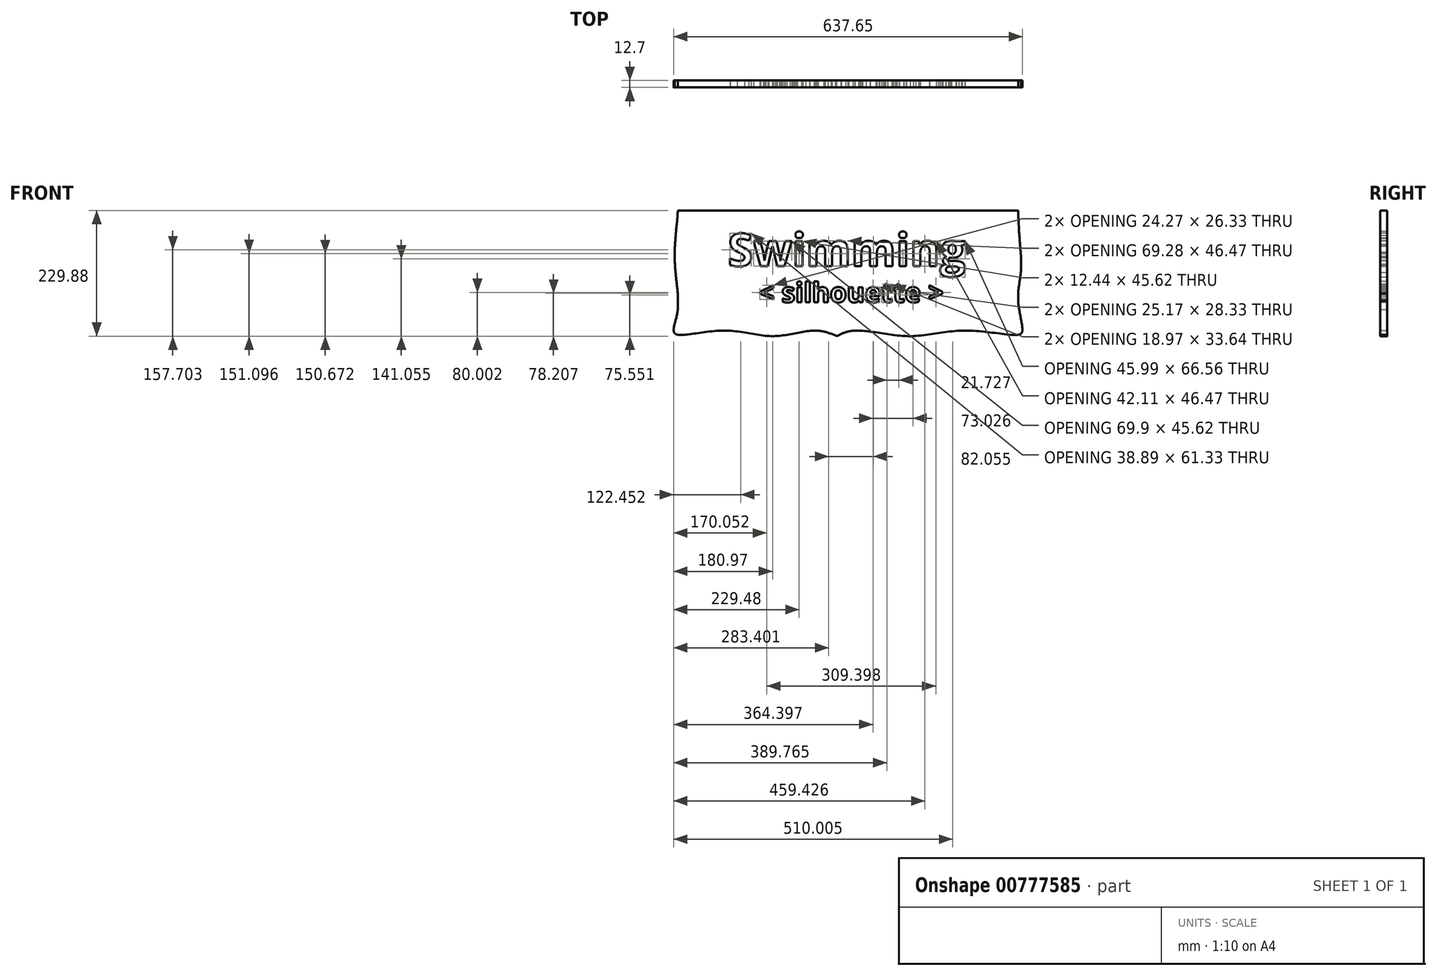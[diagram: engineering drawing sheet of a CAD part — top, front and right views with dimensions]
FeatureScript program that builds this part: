
annotation { "Feature Type Name" : "Feature", "Feature Type Description" : "" }
export const myFeature = defineFeature(function(context is Context, id is Id, definition is map)
    precondition{}
    {
        {
            var Q0;
            Q0=qCreatedBy(makeId("Front.planeOp"),FACE);
            var sketch = newSketch(context, id + "F0", { "sketchPlane" : qUnion([Q0])});
            skLineSegment(sketch, "E0.bottom", {"start": v(-290.57, 105.94) * mm, "end": v(331.73, 105.94) * mm});
            skLineSegment(sketch, "E0.top", {"start": v(-290.57, -113.77) * mm, "end": v(331.73, -113.77) * mm});
            skLineSegment(sketch, "E0.left", {"start": v(-290.57, 105.94) * mm, "end": v(-290.57, -113.77) * mm});
            skLineSegment(sketch, "E0.right", {"start": v(331.73, 105.94) * mm, "end": v(331.73, -113.77) * mm});
            skPoint(sketch, "E1", {"position": v(20.58, 105.94) * mm});
            skSolve(sketch);
        }
        {
            var Q0;
            Q0=makeQuery(id+"F0.imprint","IMPRINT",FACE,{"disambiguationData":[TD([[makeQuery(id+"F0.imprint","IMPRINT",EDGE,{"derivedFrom":sQuery(id+"F0.wireOp",EDGE,"E0.bottom")}),-1.0]])]});
            extrude(context, id + "F1", {"entities" : qUnion([Q0]), "depth" : 12.7 * mm, "offsetDistance" : 25.4 * mm});
        }
        {
            var Q0;
            Q0=makeQuery(id+"F1.opExtrude","CAP_FACE",FACE,{"disambiguationData":[OSD([sQuery(id+"F0.wireOp",EDGE,"E0.bottom"),sQuery(id+"F0.wireOp",EDGE,"E0.top"),sQuery(id+"F0.wireOp",EDGE,"E0.left"),sQuery(id+"F0.wireOp",EDGE,"E0.right")])],"isStart":false});
            var sketch = newSketch(context, id + "F2", { "sketchPlane" : qUnion([Q0])});
            skText(sketch, "E2", { "text": "Swimming", "fontName": "OpenSans-Bold.ttf"});
            const initialGuessF2  = {"E2": [-0.19905, 0.00392, 1, 0, 0.06017]};
            skSetInitialGuess(sketch, initialGuessF2);
            skSolve(sketch);
        }
        {
            var Q0;
            Q0=makeQuery(id+"F2.imprint","IMPRINT",FACE,{"disambiguationData":[TD([[makeQuery(id+"F2.imprint","IMPRINT",EDGE,{"derivedFrom":sQuery(id+"F2.wireOp",EDGE,"E2.sketch_text.stroke-0")}),1.0]])]});
            var sketch = newSketch(context, id + "F3", { "sketchPlane" : qUnion([Q0])});
            skText(sketch, "E3", { "text": " < silhouette >", "fontName": "OpenSans-Bold.ttf"});
            const initialGuessF3  = {"E3": [-0.15546, -0.06206, 1, 0, 0.03604]};
            skSetInitialGuess(sketch, initialGuessF3);
            skSolve(sketch);
        }
        {
            var Q0;
            Q0=qSketchRegion(id+"F2",true);
            var Q1;
            Q1=qSketchRegion(id+"F3",true);
            extrude(context, id + "F4", {"entities" : qUnion([Q0, Q1]), "operationType" : NewBodyOperationType.REMOVE, "oppositeDirection" : true, "depth" : 25.4 * mm, "offsetDistance" : 25.4 * mm});
        }
        {
            var Q0;
            {var subQ0=sQuery(id+"F0.wireOp",EDGE,"E0.right");var subQ1=sQuery(id+"F0.wireOp",EDGE,"E0.bottom");var subQ2=sQuery(id+"F0.wireOp",EDGE,"E0.left");var subQ3=sQuery(id+"F0.wireOp",EDGE,"E0.top");Q0=makeQuery(id+"F4.boolean.opBoolean","SPLIT",FACE,{"disambiguationData":[TD([makeQuery(id+"F1.opExtrude","SWEPT_FACE",FACE,{"disambiguationData":[OSD([subQ1])]})])],"derivedFrom":makeQuery(id+"F1.opExtrude","CAP_FACE",FACE,{"disambiguationData":[OSD([subQ1,subQ3,subQ2,subQ0])],"isStart":false})});}
            var sketch = newSketch(context, id + "F5", { "sketchPlane" : qUnion([Q0])});
            skPoint(sketch, "E4", {"position": v(-290.57, -75.67) * mm});
            skPoint(sketch, "E5", {"position": v(-290.57, 4.34) * mm});
            skPoint(sketch, "E6", {"position": v(-290.57, 74.2) * mm});
            skLineSegment(sketch, "E7", {"start": v(-290.57, 74.2) * mm, "end": v(-293.1, 74.2) * mm});
            skLineSegment(sketch, "E8", {"start": v(-290.57, 4.34) * mm, "end": v(-295.65, 4.34) * mm});
            skLineSegment(sketch, "E9", {"start": v(-290.57, -113.77) * mm, "end": v(-298.19, -113.77) * mm});
            skLineSegment(sketch, "E10", {"start": v(-290.57, -113.77) * mm, "end": v(-290.57, -121.39) * mm});
            skPoint(sketch, "E11", {"position": v(-210.29, -113.77) * mm});
            skPoint(sketch, "E12", {"position": v(0, -113.77) * mm});
            skPoint(sketch, "E13", {"position": v(-39.3, -113.77) * mm});
            skPoint(sketch, "E14", {"position": v(-115.36, -113.77) * mm});
            skPoint(sketch, "E15", {"position": v(33.42, -113.77) * mm});
            skPoint(sketch, "E16", {"position": v(131.68, -113.77) * mm});
            skPoint(sketch, "E17", {"position": v(235.49, -113.77) * mm});
            skPoint(sketch, "E18", {"position": v(331.73, -59.7) * mm});
            skPoint(sketch, "E19", {"position": v(331.73, -3.91) * mm});
            skPoint(sketch, "E20", {"position": v(331.73, 54.1) * mm});
            skLineSegment(sketch, "E21", {"start": v(331.73, 54.1) * mm, "end": v(334.27, 54.1) * mm});
            skLineSegment(sketch, "E22", {"start": v(331.73, -3.91) * mm, "end": v(336.81, -3.91) * mm});
            skLineSegment(sketch, "E23", {"start": v(331.73, -113.77) * mm, "end": v(339.35, -113.77) * mm});
            skLineSegment(sketch, "E24", {"start": v(331.73, -113.77) * mm, "end": v(331.73, -121.39) * mm});
            skLineSegment(sketch, "E25", {"start": v(-115.36, -113.77) * mm, "end": v(-115.36, -123.93) * mm});
            skLineSegment(sketch, "E26", {"start": v(0, -113.77) * mm, "end": v(0, -123.93) * mm});
            skLineSegment(sketch, "E27", {"start": v(131.68, -113.77) * mm, "end": v(131.68, -123.93) * mm});
            skFitSpline(sketch, "E28", {"points": [v(-290.57, 105.94) * mm, v(-293.1, 74.2) * mm, v(-295.65, 4.34) * mm, v(-290.57, -75.67) * mm, v(-298.19, -113.77) * mm, v(-290.57, -121.39) * mm, v(-206.79, -113.77) * mm, v(-115.36, -123.93) * mm, v(-39.3, -113.77) * mm, v(0, -123.93) * mm], "startDerivative": vector(-16.13, -484.78) * mm, "endDerivative": vector(374.15, -159.82) * mm});
            skFitSpline(sketch, "E29", {"points": [v(331.73, 105.94) * mm, v(334.27, 54.1) * mm, v(336.81, -3.91) * mm, v(331.73, -59.7) * mm, v(339.35, -113.77) * mm, v(331.73, -121.39) * mm, v(235.49, -113.77) * mm, v(131.68, -123.93) * mm, v(33.42, -113.77) * mm, v(0, -123.93) * mm], "startDerivative": vector(15.9, -475.63) * mm, "endDerivative": vector(-324.26, -164.08) * mm});
            skSolve(sketch);
        }
        {
            var Q0;
            {var subQ0=sQuery(id+"F5.wireOp",EDGE,"E26");Q0=makeQuery(id+"F5.imprint","IMPRINT",FACE,{"disambiguationData":[TD([[makeQuery(id+"F5.imprint","IMPRINT",EDGE,{"derivedFrom":subQ0}),-1.0]])]});}
            var Q1;
            {var subQ0=sQuery(id+"F5.wireOp",EDGE,"E26");Q1=makeQuery(id+"F5.imprint","IMPRINT",FACE,{"disambiguationData":[TD([[makeQuery(id+"F5.imprint","IMPRINT",EDGE,{"derivedFrom":subQ0}),1.0]])]});}
            var Q2;
            {var subQ0=sQuery(id+"F5.wireOp",EDGE,"E25");Q2=makeQuery(id+"F5.imprint","IMPRINT",FACE,{"disambiguationData":[TD([[makeQuery(id+"F5.imprint","IMPRINT",EDGE,{"derivedFrom":subQ0}),1.0]])]});}
            var Q3;
            {var subQ0=sQuery(id+"F5.wireOp",EDGE,"E25");Q3=makeQuery(id+"F5.imprint","IMPRINT",FACE,{"disambiguationData":[TD([[makeQuery(id+"F5.imprint","IMPRINT",EDGE,{"derivedFrom":subQ0}),-1.0]])]});}
            var Q4;
            {var subQ0=sQuery(id+"F5.wireOp",EDGE,"E10");Q4=makeQuery(id+"F5.imprint","IMPRINT",FACE,{"disambiguationData":[TD([[makeQuery(id+"F5.imprint","IMPRINT",EDGE,{"derivedFrom":subQ0}),1.0]])]});}
            var Q5;
            {var subQ0=sQuery(id+"F5.wireOp",EDGE,"E9");Q5=makeQuery(id+"F5.imprint","IMPRINT",FACE,{"disambiguationData":[TD([[makeQuery(id+"F5.imprint","IMPRINT",EDGE,{"derivedFrom":subQ0}),1.0]])]});}
            var Q6;
            {var subQ0=sQuery(id+"F5.wireOp",EDGE,"E9");Q6=makeQuery(id+"F5.imprint","IMPRINT",FACE,{"disambiguationData":[TD([[makeQuery(id+"F5.imprint","IMPRINT",EDGE,{"derivedFrom":subQ0}),-1.0]])]});}
            var Q7;
            {var subQ0=sQuery(id+"F5.wireOp",EDGE,"E8");Q7=makeQuery(id+"F5.imprint","IMPRINT",FACE,{"disambiguationData":[TD([[makeQuery(id+"F5.imprint","IMPRINT",EDGE,{"derivedFrom":subQ0}),1.0]])]});}
            var Q8;
            {var subQ0=sQuery(id+"F5.wireOp",EDGE,"E7");Q8=makeQuery(id+"F5.imprint","IMPRINT",FACE,{"disambiguationData":[TD([[makeQuery(id+"F5.imprint","IMPRINT",EDGE,{"derivedFrom":subQ0}),1.0]])]});}
            var Q9;
            {var subQ0=makeQuery(id+"F1.opExtrude","CAP_EDGE",EDGE,{"disambiguationData":[OSD([sQuery(id+"F0.wireOp",EDGE,"E0.bottom")])],"isStart":false});Q9=makeQuery(id+"F5.imprint","IMPRINT",FACE,{"disambiguationData":[TD([[makeQuery(id+"F5.imprint","IMPRINT",EDGE,{"derivedFrom":subQ0}),-1.0]])]});}
            var Q10;
            {var subQ0=sQuery(id+"F5.wireOp",EDGE,"E27");Q10=makeQuery(id+"F5.imprint","IMPRINT",FACE,{"disambiguationData":[TD([[makeQuery(id+"F5.imprint","IMPRINT",EDGE,{"derivedFrom":subQ0}),-1.0]])]});}
            var Q11;
            {var subQ0=sQuery(id+"F5.wireOp",EDGE,"E27");Q11=makeQuery(id+"F5.imprint","IMPRINT",FACE,{"disambiguationData":[TD([[makeQuery(id+"F5.imprint","IMPRINT",EDGE,{"derivedFrom":subQ0}),1.0]])]});}
            var Q12;
            {var subQ0=sQuery(id+"F5.wireOp",EDGE,"E24");Q12=makeQuery(id+"F5.imprint","IMPRINT",FACE,{"disambiguationData":[TD([[makeQuery(id+"F5.imprint","IMPRINT",EDGE,{"derivedFrom":subQ0}),-1.0]])]});}
            var Q13;
            {var subQ0=sQuery(id+"F5.wireOp",EDGE,"E23");Q13=makeQuery(id+"F5.imprint","IMPRINT",FACE,{"disambiguationData":[TD([[makeQuery(id+"F5.imprint","IMPRINT",EDGE,{"derivedFrom":subQ0}),-1.0]])]});}
            var Q14;
            {var subQ0=sQuery(id+"F5.wireOp",EDGE,"E23");Q14=makeQuery(id+"F5.imprint","IMPRINT",FACE,{"disambiguationData":[TD([[makeQuery(id+"F5.imprint","IMPRINT",EDGE,{"derivedFrom":subQ0}),1.0]])]});}
            var Q15;
            {var subQ0=sQuery(id+"F5.wireOp",EDGE,"E22");Q15=makeQuery(id+"F5.imprint","IMPRINT",FACE,{"disambiguationData":[TD([[makeQuery(id+"F5.imprint","IMPRINT",EDGE,{"derivedFrom":subQ0}),-1.0]])]});}
            var Q16;
            {var subQ0=sQuery(id+"F5.wireOp",EDGE,"E21");Q16=makeQuery(id+"F5.imprint","IMPRINT",FACE,{"disambiguationData":[TD([[makeQuery(id+"F5.imprint","IMPRINT",EDGE,{"derivedFrom":subQ0}),-1.0]])]});}
            var Q17;
            {var subQ0=sQuery(id+"F5.wireOp",EDGE,"E21");Q17=makeQuery(id+"F5.imprint","IMPRINT",FACE,{"disambiguationData":[TD([[makeQuery(id+"F5.imprint","IMPRINT",EDGE,{"derivedFrom":subQ0}),1.0]])]});}
            var Q18;
            {var subQ0=sQuery(id+"F5.wireOp",EDGE,"E7");Q18=makeQuery(id+"F5.imprint","IMPRINT",FACE,{"disambiguationData":[TD([[makeQuery(id+"F5.imprint","IMPRINT",EDGE,{"derivedFrom":subQ0}),-1.0]])]});}
            extrude(context, id + "F6", {"entities" : qUnion([Q0, Q1, Q2, Q3, Q4, Q5, Q6, Q7, Q8, Q9, Q10, Q11, Q12, Q13, Q14, Q15, Q16, Q17, Q18]), "operationType" : NewBodyOperationType.ADD, "depth" : -12.7 * mm, "offsetDistance" : 25.4 * mm});
        }
    });
